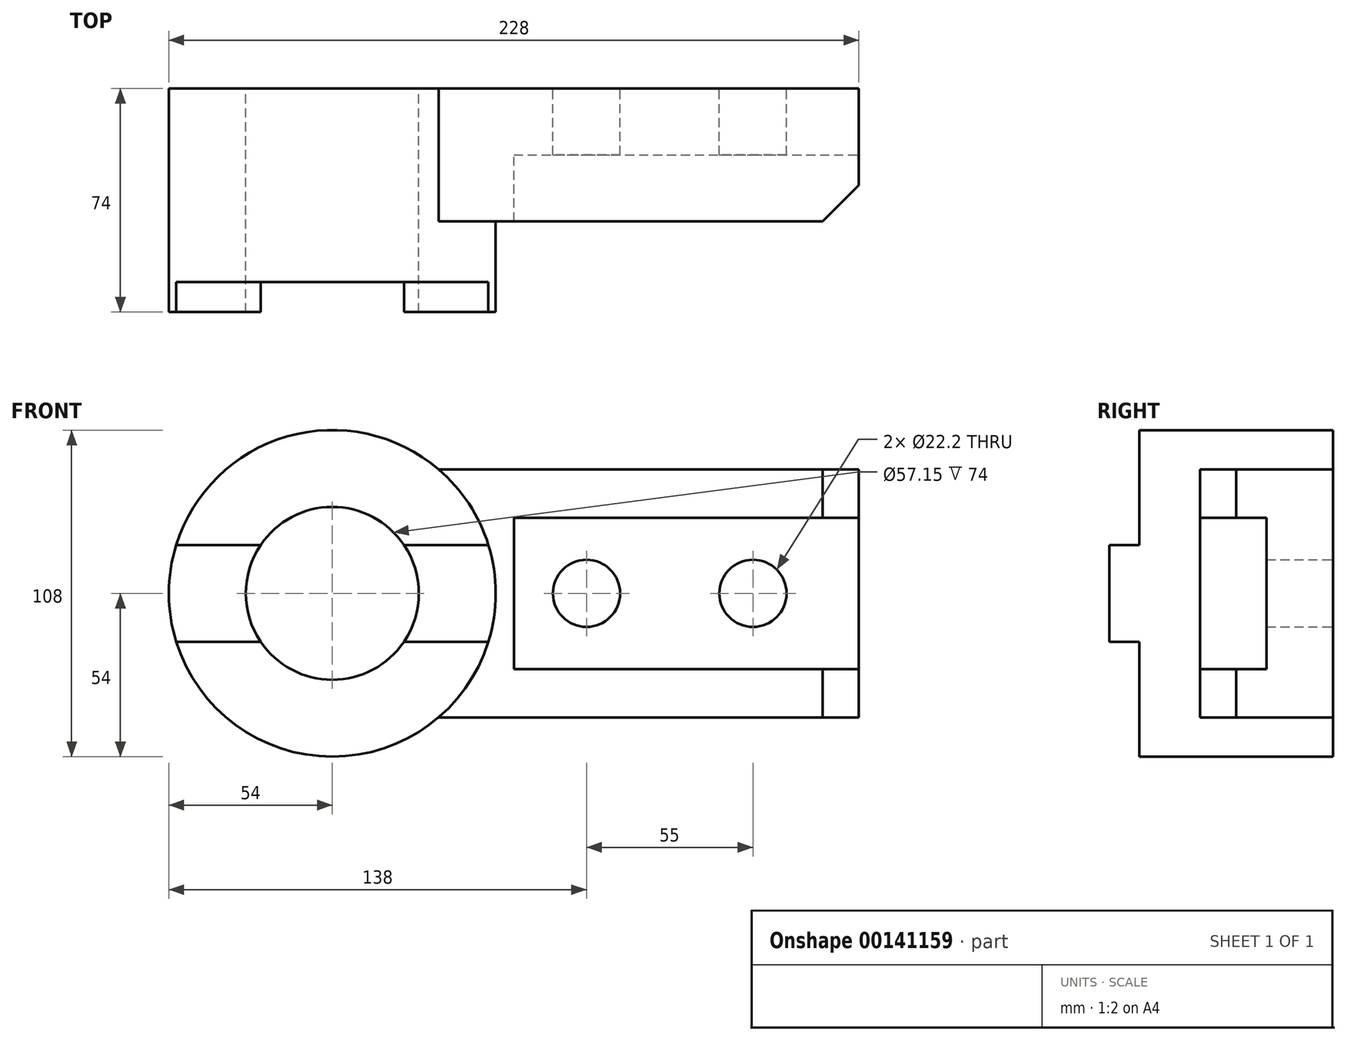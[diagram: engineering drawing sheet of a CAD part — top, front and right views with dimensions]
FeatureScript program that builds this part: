
annotation { "Feature Type Name" : "Feature", "Feature Type Description" : "" }
export const myFeature = defineFeature(function(context is Context, id is Id, definition is map)
    precondition{}
    {
        {
            var Q0;
            Q0=qCreatedBy(makeId("Front.planeOp"),FACE);
            var sketch = newSketch(context, id + "F0", { "sketchPlane" : qUnion([Q0])});
            skCircle(sketch, "E0", {"center": v(0, 0) * mm, "radius": 28.57 * mm});
            skCircle(sketch, "E1", {"center": v(0, 0) * mm, "radius": 54 * mm});
            skLineSegment(sketch, "E2", {"start": v(35.14, 41) * mm, "end": v(174, 41) * mm});
            skLineSegment(sketch, "E3", {"start": v(174, 41) * mm, "end": v(174, -41) * mm});
            skLineSegment(sketch, "E4", {"start": v(174, -41) * mm, "end": v(35.14, -41) * mm});
            skLineSegment(sketch, "E5", {"start": v(0, 0) * mm, "end": v(174, 0) * mm, "construction": true});
            skLineSegment(sketch, "E6", {"start": v(60, 25) * mm, "end": v(60, -25) * mm});
            skLineSegment(sketch, "E7", {"start": v(60, -25) * mm, "end": v(174, -25) * mm});
            skLineSegment(sketch, "E8", {"start": v(60, 25) * mm, "end": v(174, 25) * mm});
            skCircle(sketch, "E9", {"center": v(84, 0) * mm, "radius": 11.1 * mm});
            skCircle(sketch, "E10", {"center": v(139, 0) * mm, "radius": 11.1 * mm});
            skLineSegment(sketch, "E11", {"start": v(-51.58, 16) * mm, "end": v(-23.68, 16) * mm});
            skLineSegment(sketch, "E12", {"start": v(-51.58, -16) * mm, "end": v(-23.68, -16) * mm});
            skLineSegment(sketch, "E13", {"start": v(0, 0) * mm, "end": v(-54, 0) * mm, "construction": true});
            skLineSegment(sketch, "E14", {"start": v(-23.68, 16) * mm, "end": v(-23.68, -16) * mm, "construction": true});
            skLineSegment(sketch, "E15", {"start": v(23.68, 16) * mm, "end": v(51.58, 16) * mm});
            skLineSegment(sketch, "E16", {"start": v(23.68, -16) * mm, "end": v(51.58, -16) * mm});
            skSolve(sketch);
        }
        {
            var Q0;
            {var subQ0=sQuery(id+"F0.wireOp",EDGE,"E2");Q0=makeQuery(id+"F0.imprint","IMPRINT",FACE,{"disambiguationData":[TD([[makeQuery(id+"F0.imprint","IMPRINT",EDGE,{"derivedFrom":subQ0}),-1.0]])]});}
            extrude(context, id + "F1", {"entities" : qUnion([Q0]), "depth" : 44 * mm});
        }
        {
            var Q0;
            Q0=makeQuery(id+"F0.imprint","IMPRINT",FACE,{"disambiguationData":[TD([[makeQuery(id+"F0.imprint","IMPRINT",EDGE,{"derivedFrom":sQuery(id+"F0.wireOp",EDGE,"E6")}),1.0]])]});
            extrude(context, id + "F2", {"entities" : qUnion([Q0]), "operationType" : NewBodyOperationType.ADD, "depth" : 22 * mm});
        }
        {
            var Q0;
            {var subQ0=sQuery(id+"F0.wireOp",EDGE,"E11");Q0=makeQuery(id+"F0.imprint","IMPRINT",FACE,{"disambiguationData":[TD([[makeQuery(id+"F0.imprint","IMPRINT",EDGE,{"derivedFrom":subQ0}),1.0]])]});}
            var Q1;
            {var subQ3=sQuery(id+"F0.wireOp",EDGE,"E12");Q1=makeQuery(id+"F0.imprint","IMPRINT",FACE,{"disambiguationData":[TD([[makeQuery(id+"F0.imprint","IMPRINT",EDGE,{"derivedFrom":subQ3}),-1.0]])]});}
            extrude(context, id + "F3", {"entities" : qUnion([Q0, Q1]), "operationType" : NewBodyOperationType.ADD, "depth" : 64 * mm});
        }
        {
            var Q0;
            {var subQ0=sQuery(id+"F0.wireOp",EDGE,"E15");Q0=makeQuery(id+"F0.imprint","IMPRINT",FACE,{"disambiguationData":[TD([[makeQuery(id+"F0.imprint","IMPRINT",EDGE,{"derivedFrom":subQ0}),-1.0]])]});}
            var Q1;
            {var subQ0=sQuery(id+"F0.wireOp",EDGE,"E11");Q1=makeQuery(id+"F0.imprint","IMPRINT",FACE,{"disambiguationData":[TD([[makeQuery(id+"F0.imprint","IMPRINT",EDGE,{"derivedFrom":subQ0}),-1.0]])]});}
            extrude(context, id + "F4", {"entities" : qUnion([Q0, Q1]), "operationType" : NewBodyOperationType.ADD, "depth" : 74 * mm});
        }
        {
            var Q0;
            {var subQ0=sQuery(id+"F0.wireOp",EDGE,"E3");Q0=makeQuery(id+"F1.opExtrude","CAP_EDGE",EDGE,{"disambiguationData":[OSD([subQ0]),TDD([makeQuery(id+"F0.imprint","IMPRINT",EDGE,{"disambiguationData":[TD([[makeQuery(id+"F0.imprint","INTERSECT",VERTEX,{"derivedFrom":[subQ0,sQuery(id+"F0.wireOp",EDGE,"E4")]}),1.0]])],"derivedFrom":subQ0})])],"isStart":false});}
            var Q1;
            {var subQ0=sQuery(id+"F0.wireOp",EDGE,"E3");Q1=makeQuery(id+"F1.opExtrude","CAP_EDGE",EDGE,{"disambiguationData":[OSD([subQ0]),TDD([makeQuery(id+"F0.imprint","IMPRINT",EDGE,{"disambiguationData":[TD([[makeQuery(id+"F0.imprint","INTERSECT",VERTEX,{"derivedFrom":[sQuery(id+"F0.wireOp",EDGE,"E2"),subQ0]}),-1.0]])],"derivedFrom":subQ0})])],"isStart":false});}
            chamfer(context, id + "F5", {"entities" : qUnion([Q0, Q1]), "chamferType" : ChamferType.OFFSET_ANGLE, "width" : 12 * mm, "oppositeDirection" : false, "angle" : 45 * degree, "tangentPropagation" : true});
        }
    });
